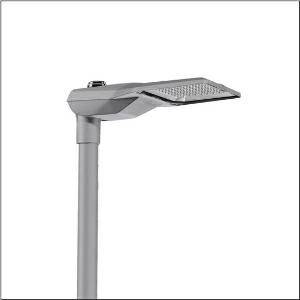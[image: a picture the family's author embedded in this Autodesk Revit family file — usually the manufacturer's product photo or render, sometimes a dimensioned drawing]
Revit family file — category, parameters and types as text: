
# Revit family: streetlight_sl_21_midi___st1_0a_5xe7d67n08mb_a1db
name_source: partatom
category: Lighting Fixtures
units: mm (PartAtom-declared; Revit-internal decimal feet)

## family parameters
Cut with Voids When Loaded = No
Host = Face
Light Source = No
Part Type = Normal
Room Calculation Point = No
Round Connector Dimension = Use Diameter
Shared = No

## types (1)
- --- (1 x LED, 16240 lm, 134.3 W, 2700K)
    Apparent Load = 134 VA
    CIE Flux Codes = 37 72 97 100 100
    Color Rendering = 70
    Color Temperature = 2700K
    Default Elevation = 1800 mm
    Description = Streetlight SL 21 midi, mast luminaire, primary light control with lens, of PMMA, primary optical cover: cover, of toughened safety glass, transparent, light distribution: ST1.0a, light emission: direct distribution, primary light characteristic: asymmetric, installation type: side-entry, LED, 3G 2.5mm², High Power LED, rated luminous flux: 16.240lm, luminous efficacy: 121lm/W, light colour: 727, colour temperature: 2700K, control: overheat protection, presetting dimming linear, constant luminous flux control, time-dependent luminous flux control, flexible luminous flux parameterisation, mains connection: 220..240V, AC, 50/60Hz, connection cable pre-assembled, cable length: 12,5m, wiring characteristics: H05VV-F, start of lifetime: 134W, end of service life: 141W, reduction: 60W, luminaire housing, of diecast aluminium (EN AC-44300), powder-coated, Siteco® metallic grey (DB 702S), corrosivity category C5 mid according to DIN EN ISO 12944, multi-level sealing system, sealing non-destructively replaceable, inclination adjustable: 0°, 5°, 10°, 15°, length: 644mm, width: 335mm, height: 110mm, spigot size: 42mm (side-entry), protection rating (complete): IP66, insulation class (complete): insulation class I (protective earthing), certification: CE, ENEC, ENEC+, VDE, impact resistance: IK09, permissible operating ambient temperature for outdoor applications: -40..+50°C, standard-compliant lighting for roads and squares, packaging unit: 1 piece

Light Distribution: ST1.0a
    Height = 111 mm
    Lamp = 1 x LED
    Lamp Light Flux = 16240 lm
    Lamp Power = 134.3 W
    Lamp count = 1
    Length = 644 mm
    Luminous efficacy = 121 lm/W
    Manufacturer = Siteco
    ModVariant = No
    Model = 5XE7D67N08MB
    Number of Poles = 1
    OnlyDefault = Yes
    Power Factor = 1
    Product Name = Streetlight SL 21 midi | ST1.0a
    Product group = mast luminaire | pylon top
    ProductGroupID = 6100
    Protection Class = Protection class I
    Protection Degree = IP 66
    RLX_Detail_Level = 1
    RLX_Emergency_Light_Flux = 0 lm
    RLX_Emergency_Type = 0
    RLX_Emergency_Type_DB = No
    RlxData = <blob elided: 90129 chars, md5=5b0e5e2b>
    Socket = socket
    Standby Power = 0 W
    System Light Flux = 16240 lm
    System Power = 134 W
    Type Comments = factory setting: luminous flux: 100 % | dim-lin: 254 | 687 mA
    Type Image = l_1294377.jpg
    URL = http://relux.com
    VarID = @adj_067227
    Voltage = 0 V
    Weight = 0.00 kg
    Width = 336 mm

## geometry (parser evidence)
native form markers: Blend x4, Sweep x11
no freeform markers — native parametric forms only
